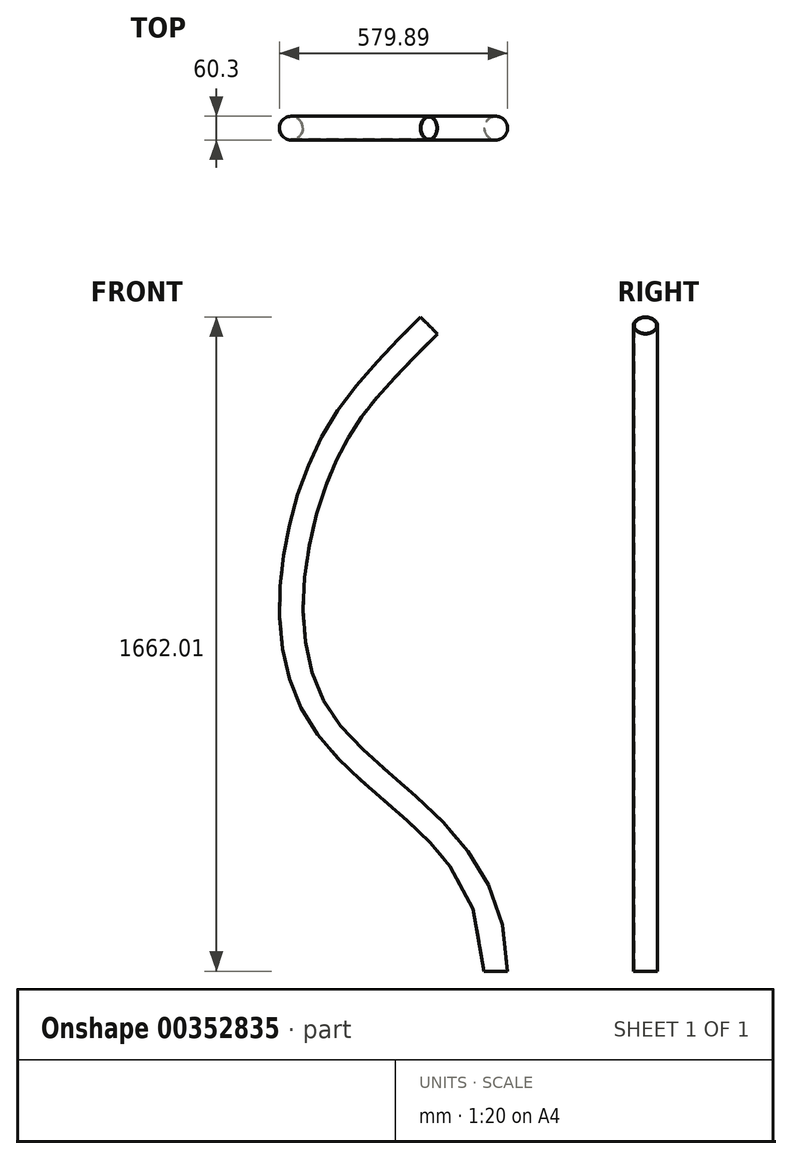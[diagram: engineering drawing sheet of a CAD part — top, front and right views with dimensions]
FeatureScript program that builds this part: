
annotation { "Feature Type Name" : "Feature", "Feature Type Description" : "" }
export const myFeature = defineFeature(function(context is Context, id is Id, definition is map)
    precondition{}
    {
        {
            var Q0;
            Q0=qCreatedBy(makeId("Front.planeOp"),FACE);
            var sketch = newSketch(context, id + "F0", { "sketchPlane" : qUnion([Q0])});
            skFitSpline(sketch, "E0", {"points": [v(0, 0) * mm, v(-450, 650) * mm, v(-450.65, 1268.56) * mm, v(-169.7, 1640.69) * mm], "startDerivative": vector(0, 2785.16) * mm, "endDerivative": vector(1420.91, 1420.91) * mm});
            skSolve(sketch);
        }
        {
            var Q0;
            Q0=qCreatedBy(makeId("Top.planeOp"),FACE);
            var sketch = newSketch(context, id + "F1", { "sketchPlane" : qUnion([Q0])});
            skCircle(sketch, "E1", {"center": v(0, 0) * mm, "radius": 30.15 * mm});
            skCircle(sketch, "E2", {"center": v(0, 0) * mm, "radius": 28.5 * mm});
            skSolve(sketch);
        }
        {
            var Q0;
            Q0=makeQuery(id+"F1.imprint","IMPRINT",FACE,{"disambiguationData":[TD([[makeQuery(id+"F1.imprint","IMPRINT",EDGE,{"derivedFrom":sQuery(id+"F1.wireOp",EDGE,"E1")}),1.0]])]});
            var Q1;
            Q1=sQuery(id+"F0.wireOp",EDGE,"E0");
            sweep(context, id + "F2", {"profiles" : qUnion([Q0]), "path" : qUnion([Q1])});
        }
    });
